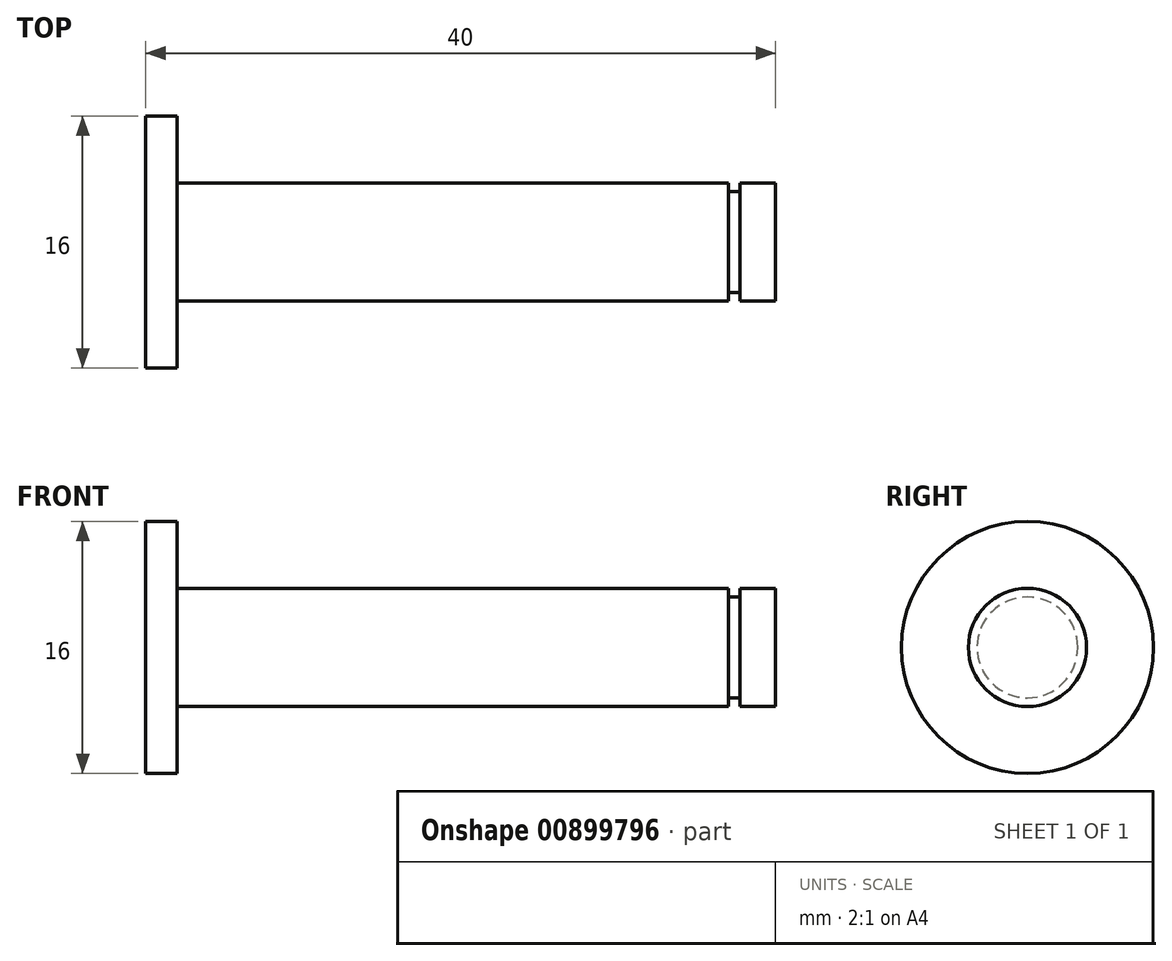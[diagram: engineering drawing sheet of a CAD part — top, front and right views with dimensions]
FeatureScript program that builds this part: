
annotation { "Feature Type Name" : "Feature", "Feature Type Description" : "" }
export const myFeature = defineFeature(function(context is Context, id is Id, definition is map)
    precondition{}
    {
        {
            var Q0;
            Q0=qCreatedBy(makeId("Front.planeOp"),FACE);
            var sketch = newSketch(context, id + "F0", { "sketchPlane" : qUnion([Q0])});
            skLineSegment(sketch, "E0", {"start": v(0, 0) * mm, "end": v(0, 8) * mm});
            skLineSegment(sketch, "E1", {"start": v(0, 8) * mm, "end": v(2, 8) * mm});
            skLineSegment(sketch, "E2", {"start": v(2, 8) * mm, "end": v(2, 3.75) * mm});
            skLineSegment(sketch, "E3", {"start": v(2, 3.75) * mm, "end": v(37, 3.75) * mm});
            skLineSegment(sketch, "E4", {"start": v(37, 3.75) * mm, "end": v(37, 3.2) * mm});
            skLineSegment(sketch, "E5", {"start": v(37, 3.2) * mm, "end": v(37.73, 3.2) * mm});
            skLineSegment(sketch, "E6", {"start": v(37.73, 3.2) * mm, "end": v(37.73, 3.75) * mm});
            skLineSegment(sketch, "E7", {"start": v(37.73, 3.75) * mm, "end": v(40, 3.75) * mm});
            skLineSegment(sketch, "E8", {"start": v(40, 3.75) * mm, "end": v(40, 0) * mm});
            skLineSegment(sketch, "E9", {"start": v(40, 0) * mm, "end": v(0, 0) * mm});
            skSolve(sketch);
        }
        {
            var Q0;
            Q0 = qSketchRegion(id + "F0", true);
            var Q1;
            Q1=sQuery(id+"F0.wireOp",EDGE,"E9");
            revolve(context, id + "F1", {"surfaceOperationType" : NewSurfaceOperationType.NEW, "entities" : qUnion([Q0]), "axis" : qUnion([Q1]), "revolveType" : RevolveType.FULL});
        }
    });
